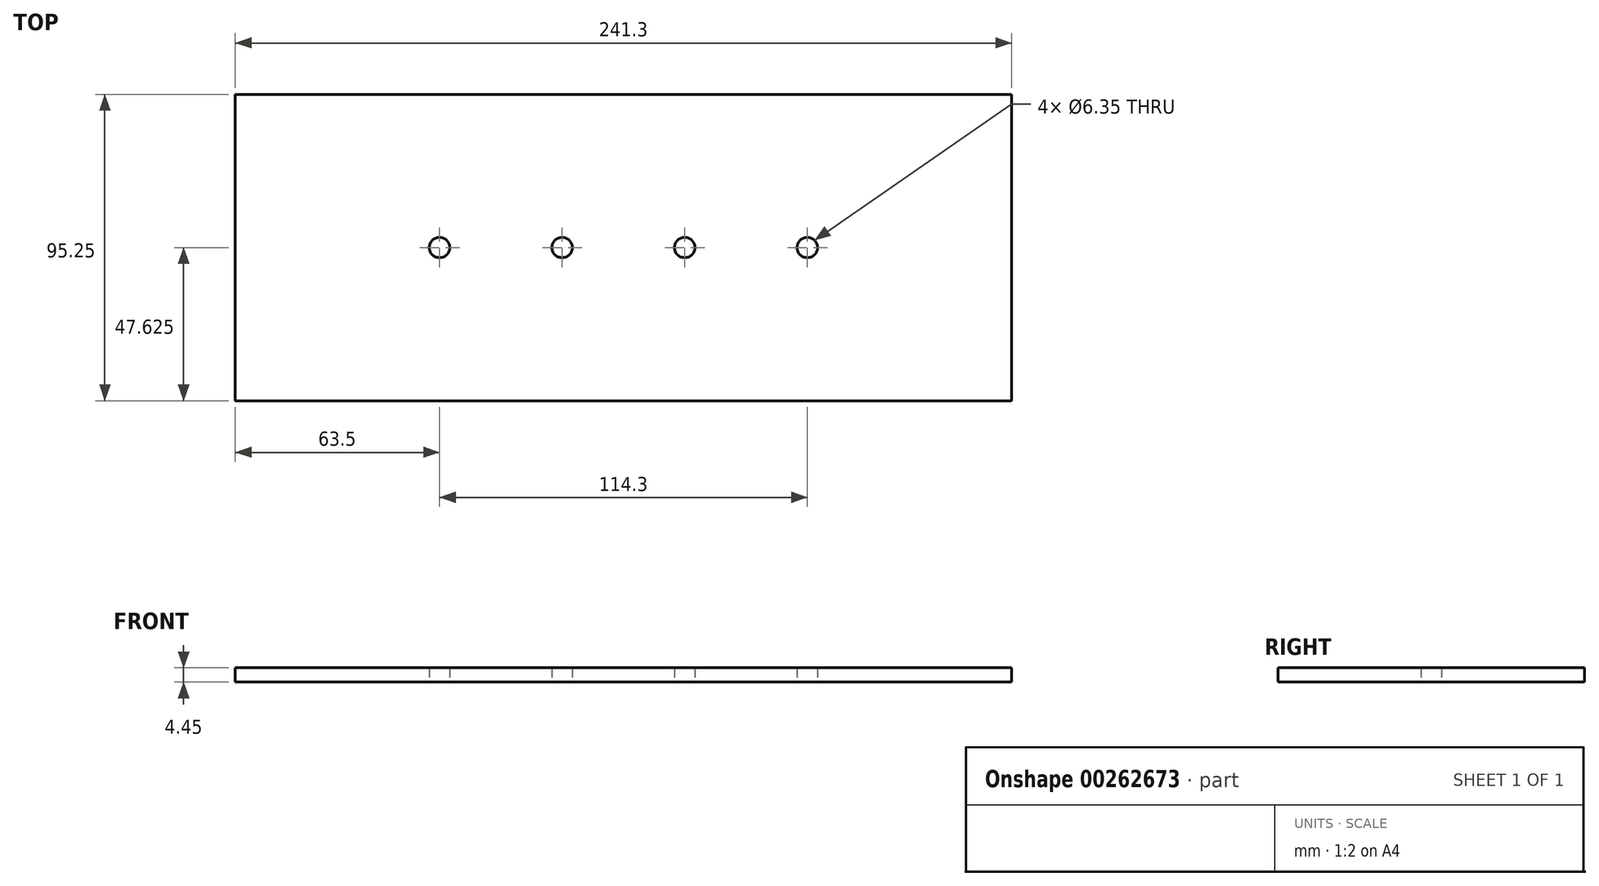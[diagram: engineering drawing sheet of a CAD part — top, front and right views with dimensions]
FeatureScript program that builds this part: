
annotation { "Feature Type Name" : "Feature", "Feature Type Description" : "" }
export const myFeature = defineFeature(function(context is Context, id is Id, definition is map)
    precondition{}
    {
        {
            var Q0;
            Q0=qCreatedBy(makeId("Top.planeOp"),FACE);
            var sketch = newSketch(context, id + "F0", { "sketchPlane" : qUnion([Q0])});
            skLineSegment(sketch, "E0.bottom", {"start": v(0, 0) * mm, "end": v(241.3, 0) * mm});
            skLineSegment(sketch, "E0.top", {"start": v(0, 95.25) * mm, "end": v(241.3, 95.25) * mm});
            skLineSegment(sketch, "E0.left", {"start": v(0, 0) * mm, "end": v(0, 95.25) * mm});
            skLineSegment(sketch, "E0.right", {"start": v(241.3, 0) * mm, "end": v(241.3, 95.25) * mm});
            skCircle(sketch, "E1", {"center": v(63.5, 47.63) * mm, "radius": 3.17 * mm});
            skPoint(sketch, "E1.centerSnap0", {"position": v(0, 47.63) * mm});
            skCircle(sketch, "E2", {"center": v(101.6, 47.63) * mm, "radius": 3.18 * mm});
            skCircle(sketch, "E3", {"center": v(139.7, 47.63) * mm, "radius": 3.18 * mm});
            skCircle(sketch, "E4", {"center": v(177.8, 47.63) * mm, "radius": 3.18 * mm});
            skSolve(sketch);
        }
        {
            var Q0;
            Q0=makeQuery(id+"F0.imprint","IMPRINT",FACE,{"disambiguationData":[TD([[makeQuery(id+"F0.imprint","IMPRINT",EDGE,{"derivedFrom":sQuery(id+"F0.wireOp",EDGE,"E0.bottom")}),1.0]])]});
            extrude(context, id + "F1", {"entities" : qUnion([Q0]), "depth" : 4.44 * mm});
        }
    });
